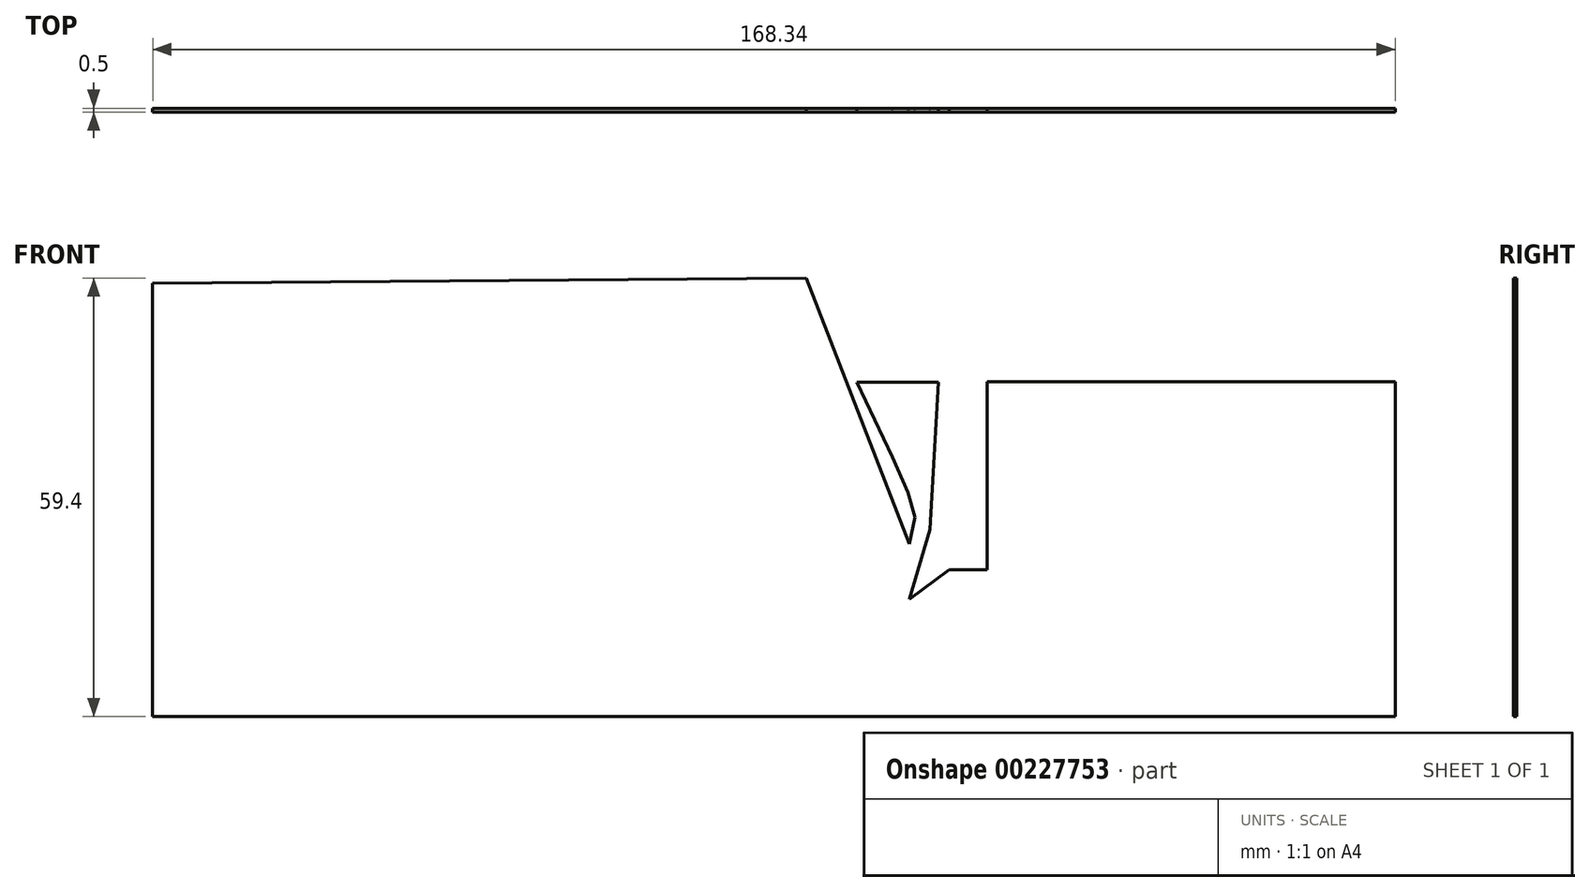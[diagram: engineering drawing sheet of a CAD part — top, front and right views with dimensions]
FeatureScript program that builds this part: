
annotation { "Feature Type Name" : "Feature", "Feature Type Description" : "" }
export const myFeature = defineFeature(function(context is Context, id is Id, definition is map)
    precondition{}
    {
        {
            var Q0;
            Q0=qCreatedBy(makeId("Front.planeOp"),FACE);
            var sketch = newSketch(context, id + "F0", { "sketchPlane" : qUnion([Q0])});
            skLineSegment(sketch, "E0", {"start": v(-45.16, -34.25) * mm, "end": v(-46.3, -54.18) * mm});
            skLineSegment(sketch, "E1", {"start": v(-46.3, -54.18) * mm, "end": v(-49.08, -63.64) * mm});
            skLineSegment(sketch, "E2", {"start": v(-49.08, -63.64) * mm, "end": v(-43.68, -59.67) * mm});
            skLineSegment(sketch, "E3", {"start": v(16.75, -34.15) * mm, "end": v(16.75, -62.32) * mm});
            skLineSegment(sketch, "E4.top", {"start": v(16.75, -79.54) * mm, "end": v(-144.15, -79.54) * mm});
            skLineSegment(sketch, "E4.left", {"start": v(16.75, -62.32) * mm, "end": v(16.75, -79.54) * mm});
            skLineSegment(sketch, "E5", {"start": v(-151.6, -20.82) * mm, "end": v(-151.6, -79.54) * mm});
            skLineSegment(sketch, "E6", {"start": v(-151.6, -79.54) * mm, "end": v(-144.15, -79.54) * mm});
            skLineSegment(sketch, "E7", {"start": v(-56.2, -34.25) * mm, "end": v(-45.16, -34.25) * mm});
            skLineSegment(sketch, "E8", {"start": v(-49.08, -56.18) * mm, "end": v(-63.05, -20.14) * mm});
            skLineSegment(sketch, "E9", {"start": v(-48.3, -52.52) * mm, "end": v(-49.08, -56.18) * mm});
            skLineSegment(sketch, "E10", {"start": v(-38.55, -34.15) * mm, "end": v(16.75, -34.15) * mm});
            skLineSegment(sketch, "E11", {"start": v(-63.05, -20.14) * mm, "end": v(-151.6, -20.82) * mm});
            skLineSegment(sketch, "E12", {"start": v(-56.2, -34.25) * mm, "end": v(-51.39, -44.4) * mm});
            skLineSegment(sketch, "E13", {"start": v(-51.39, -44.4) * mm, "end": v(-49.24, -49.19) * mm});
            skLineSegment(sketch, "E14", {"start": v(-49.24, -49.19) * mm, "end": v(-48.3, -52.52) * mm});
            skLineSegment(sketch, "E15", {"start": v(-38.55, -34.15) * mm, "end": v(-38.55, -59.67) * mm});
            skLineSegment(sketch, "E16", {"start": v(-38.55, -59.67) * mm, "end": v(-43.68, -59.67) * mm});
            skSolve(sketch);
        }
        {
            var Q0;
            Q0 = qSketchRegion(id + "F0", true);
            extrude(context, id + "F1", {"entities" : qUnion([Q0]), "depth" : 0.5 * mm});
        }
    });
